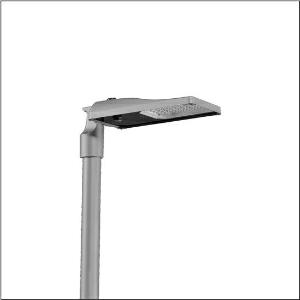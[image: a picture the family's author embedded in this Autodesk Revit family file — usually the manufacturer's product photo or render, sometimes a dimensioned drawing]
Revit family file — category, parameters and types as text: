
# Revit family: streetlight_sl_31_mini___st1_0a_5xh2d31t08ga_2aba
name_source: partatom
category: Lighting Fixtures
units: mm (PartAtom-declared; Revit-internal decimal feet)

## family parameters
Cut with Voids When Loaded = No
Host = Face
Light Source = No
Part Type = Normal
Room Calculation Point = No
Round Connector Dimension = Use Diameter
Shared = No

## types (1)
- --- (1 x LED, 5880 lm, 39.3 W, 3000K)
    Apparent Load = 39 VA
    CIE Flux Codes = 37 72 97 100 100
    Color Rendering = 70
    Color Temperature = 3000K
    Default Elevation = 1800 mm
    Description = Streetlight SL 31 mini, mast luminaire, primary light control with lens, of PMMA, primary optical cover: cover, of toughened safety glass, transparent, light distribution: ST1.0a, light emission: direct distribution, primary light characteristic: asymmetric, installation type: post-top, side-entry, LED, High Power LED, rated luminous flux: 5.880lm, luminous efficacy: 150lm/W, light colour: 730, colour temperature: 3000K, control: presetting dimming logarithmic, flexible luminous flux parameterisation, time-dependent luminous flux control, constant luminous flux control, power reduction, intelligent temperature release in ECG and LED module, overheat protection, with cable H07RN-F 2x 1.5mm², mains connection: 220..240V, AC, 50/60Hz, connection cable pre-assembled, cable length: 6,5m, start of lifetime: 39W, end of service life: 41W, reduction: 18W, luminaire housing, of diecast aluminium, powder-coated, Siteco® metallic grey (DB 702S), corrosivity category C5 high according to DIN EN ISO 12944, no sealing on luminaire upper side, inclination: -15°..+20° (post-top) | -20°..+20° (side-entry), adjustable in 5° steps, mast flange (76/60mm) included as standard, multi-level sealing system, sealing non-destructively replaceable, Smart Interface below and above, protection rating (complete): IP66, insulation class (complete): insulation class II (safety insulation), certification: CE, ENEC, ENEC+, VDE, UKCA, ZD4i, impact resistance: IK09, permissible operating ambient temperature for outdoor applications: -40..+50°C, standard-compliant lighting for roads and squares, packaging unit: 1 piece

Light Distribution: ST1.0a
    Height = 76 mm
    Lamp = 1 x LED
    Lamp Light Flux = 5880 lm
    Lamp Power = 39.3 W
    Lamp count = 1
    Length = 547 mm
    Luminous efficacy = 150 lm/W
    Manufacturer = Siteco
    ModVariant = No
    Model = 5XH2D31T08GA
    Number of Poles = 1
    OnlyDefault = Yes
    Power Factor = 1
    Product Name = Streetlight SL 31 mini | ST1.0a
    Product group = mast luminaire | pylon top
    ProductGroupID = 6100
    Protection Class = Protection class II
    Protection Degree = IP 66
    RLX_Detail_Level = 1
    RLX_Emergency_Light_Flux = 0 lm
    RLX_Emergency_Type = 0
    RLX_Emergency_Type_DB = No
    RlxData = <blob elided: 40193 chars, md5=66197bf3>
    Socket = socket
    Standby Power = 0 W
    System Light Flux = 5880 lm
    System Power = 39 W
    Type Comments = factory setting: luminous flux: 100 % | dim-lin: 254 | 798 mA
    Type Image = l_1300332.jpg
    URL = http://relux.com
    VarID = @adj_012923
    Voltage = 0 V
    Weight = 0.00 kg
    Width = 265 mm

## geometry (parser evidence)
native form markers: Blend x4, Sweep x10
no freeform markers — native parametric forms only
